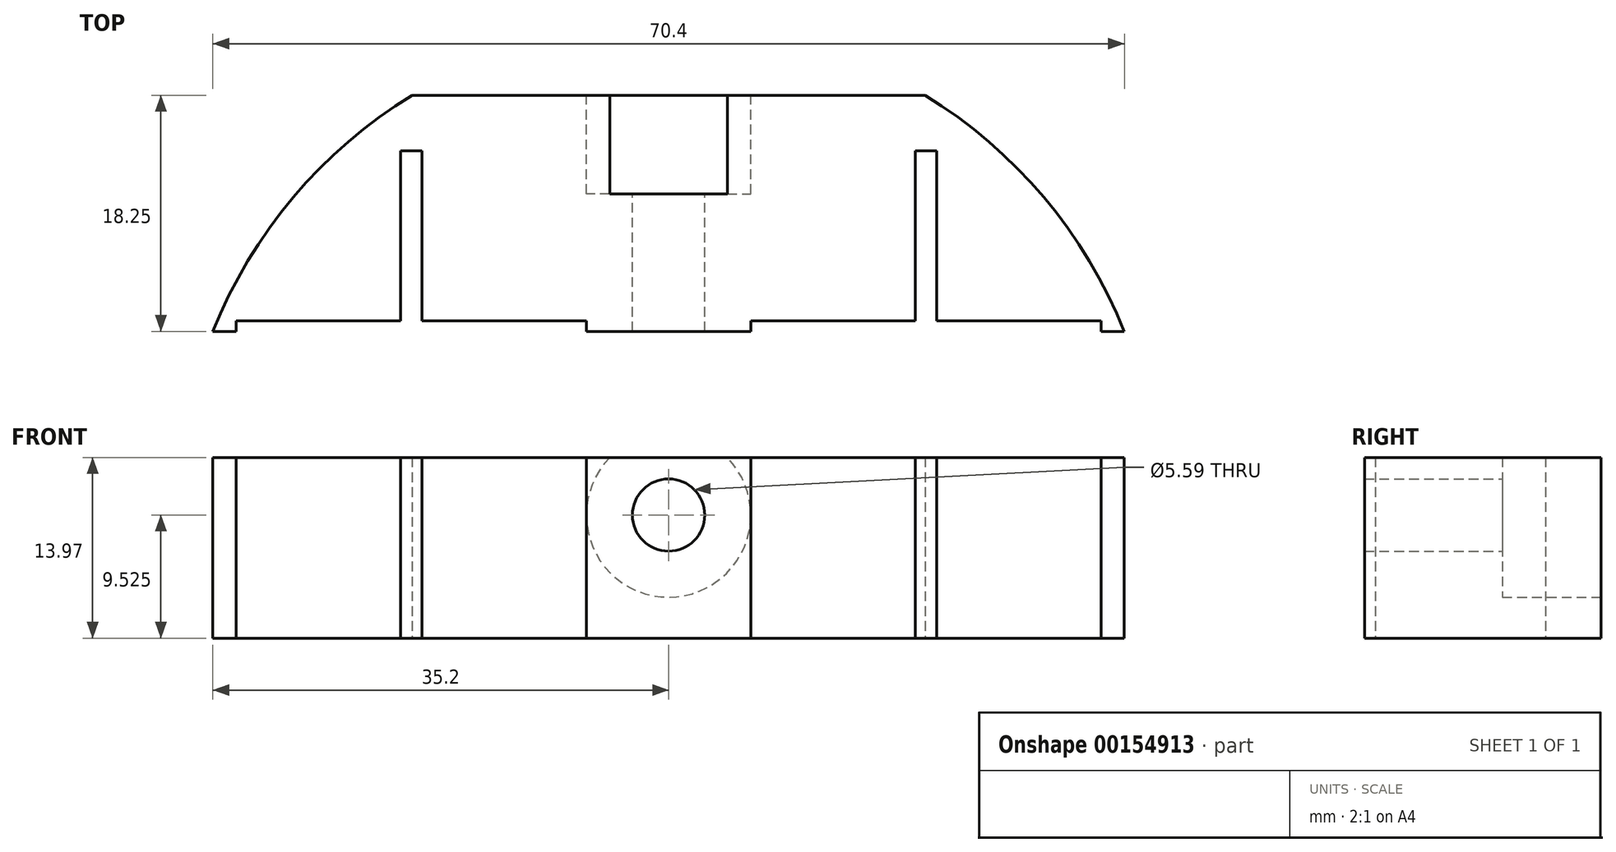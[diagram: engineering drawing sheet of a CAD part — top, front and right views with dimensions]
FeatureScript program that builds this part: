
annotation { "Feature Type Name" : "Feature", "Feature Type Description" : "" }
export const myFeature = defineFeature(function(context is Context, id is Id, definition is map)
    precondition{}
    {
        {
            var Q0;
            Q0=qCreatedBy(makeId("Top.planeOp"),FACE);
            var sketch = newSketch(context, id + "F0", { "sketchPlane" : qUnion([Q0])});
            skArc(sketch, "E0", {"start": v(-19.82, 32.3) * mm, "mid": v(-28.98, 24.42) * mm, "end": v(-35.2, 14.05) * mm});
            skLineSegment(sketch, "E1", {"start": v(-35.2, 14.05) * mm, "end": v(-33.4, 14.05) * mm});
            skLineSegment(sketch, "E2", {"start": v(0, 14.05) * mm, "end": v(0, 32.3) * mm});
            skLineSegment(sketch, "E3", {"start": v(-19.82, 32.3) * mm, "end": v(0, 32.3) * mm});
            skLineSegment(sketch, "E4", {"start": v(-33.4, 14.05) * mm, "end": v(-33.4, 14.87) * mm});
            skLineSegment(sketch, "E5", {"start": v(-33.4, 14.87) * mm, "end": v(-20.7, 14.87) * mm});
            skLineSegment(sketch, "E6", {"start": v(-20.7, 14.87) * mm, "end": v(-20.7, 28.02) * mm});
            skLineSegment(sketch, "E7", {"start": v(-20.7, 28.02) * mm, "end": v(-19.05, 28.02) * mm});
            skLineSegment(sketch, "E8", {"start": v(-19.05, 28.02) * mm, "end": v(-19.05, 14.87) * mm});
            skLineSegment(sketch, "E9", {"start": v(-19.05, 14.87) * mm, "end": v(-6.35, 14.87) * mm});
            skLineSegment(sketch, "E10", {"start": v(-6.35, 14.87) * mm, "end": v(-6.35, 14.05) * mm});
            skLineSegment(sketch, "E11.trimOffspring", {"start": v(-6.35, 14.05) * mm, "end": v(0, 14.05) * mm});
            skSolve(sketch);
        }
        {
            var Q0;
            Q0=makeQuery(id+"F0.imprint","IMPRINT",FACE,{"disambiguationData":[TD([[makeQuery(id+"F0.imprint","IMPRINT",EDGE,{"derivedFrom":sQuery(id+"F0.wireOp",EDGE,"E0")}),1.0]])]});
            extrude(context, id + "F1", {"entities" : qUnion([Q0]), "depth" : 19.05 * mm});
        }
        {
            var Q0;
            Q0=makeQuery(id+"F1.opExtrude","SWEPT_BODY",BODY,{"disambiguationData":[OSD([sQuery(id+"F0.wireOp",EDGE,"E0"),sQuery(id+"F0.wireOp",EDGE,"E1"),sQuery(id+"F0.wireOp",EDGE,"E2"),sQuery(id+"F0.wireOp",EDGE,"E3"),sQuery(id+"F0.wireOp",EDGE,"E4"),sQuery(id+"F0.wireOp",EDGE,"E5"),sQuery(id+"F0.wireOp",EDGE,"E6"),sQuery(id+"F0.wireOp",EDGE,"E7"),sQuery(id+"F0.wireOp",EDGE,"E8"),sQuery(id+"F0.wireOp",EDGE,"E9"),sQuery(id+"F0.wireOp",EDGE,"E10"),sQuery(id+"F0.wireOp",EDGE,"E11.trimOffspring")])]});
            var Q1;
            Q1=qCreatedBy(makeId("Right.planeOp"),FACE);
            mirror(context, id + "F2", {"operationType" : NewBodyOperationType.ADD, "entities" : qUnion([Q0]), "mirrorPlane" : qUnion([Q1])});
        }
        {
            var Q0;
            {var subQ0=makeQuery(id+"F1.opExtrude","SWEPT_FACE",FACE,{"disambiguationData":[OSD([sQuery(id+"F0.wireOp",EDGE,"E3")])]});Q0=makeQuery(id+"F2.boolean.opBoolean","MERGE",FACE,{"derivedFrom":[subQ0,makeQuery(id+"F2.opPattern","COPY",FACE,{"derivedFrom":subQ0,"instanceName":"1"})]});}
            var sketch = newSketch(context, id + "F3", { "sketchPlane" : qUnion([Q0])});
            skLineSegment(sketch, "E12", {"start": v(0, 19.05) * mm, "end": v(0, 0) * mm, "construction": true});
            skLineSegment(sketch, "E13", {"start": v(19.82, 9.53) * mm, "end": v(-19.82, 9.53) * mm, "construction": true});
            skCircle(sketch, "E14", {"center": v(0, 9.53) * mm, "radius": 2.8 * mm});
            skSolve(sketch);
        }
        {
            var Q0;
            Q0 = qSketchRegion(id + "F3", true);
            extrude(context, id + "F4", {"entities" : qUnion([Q0]), "operationType" : NewBodyOperationType.REMOVE, "endBound" : BoundingType.UP_TO_NEXT, "oppositeDirection" : true, "depth" : 25.4 * mm});
        }
        {
            var Q0;
            {var subQ0=makeQuery(id+"F1.opExtrude","SWEPT_FACE",FACE,{"disambiguationData":[OSD([sQuery(id+"F0.wireOp",EDGE,"E3")])]});Q0=makeQuery(id+"F2.boolean.opBoolean","MERGE",FACE,{"derivedFrom":[subQ0,makeQuery(id+"F2.opPattern","COPY",FACE,{"derivedFrom":subQ0,"instanceName":"1"})]});}
            var sketch = newSketch(context, id + "F5", { "sketchPlane" : qUnion([Q0])});
            skCircle(sketch, "E15", {"center": v(0, 9.53) * mm, "radius": 6.35 * mm});
            skSolve(sketch);
        }
        {
            var Q0;
            Q0 = qSketchRegion(id + "F5", true);
            extrude(context, id + "F6", {"entities" : qUnion([Q0]), "operationType" : NewBodyOperationType.REMOVE, "oppositeDirection" : true, "depth" : 7.62 * mm});
        }
        {
            var Q0;
            {var subQ0=makeQuery(id+"F1.opExtrude","CAP_FACE",FACE,{"disambiguationData":[OSD([sQuery(id+"F0.wireOp",EDGE,"E0"),sQuery(id+"F0.wireOp",EDGE,"E1"),sQuery(id+"F0.wireOp",EDGE,"E2"),sQuery(id+"F0.wireOp",EDGE,"E3"),sQuery(id+"F0.wireOp",EDGE,"E4"),sQuery(id+"F0.wireOp",EDGE,"E5"),sQuery(id+"F0.wireOp",EDGE,"E6"),sQuery(id+"F0.wireOp",EDGE,"E7"),sQuery(id+"F0.wireOp",EDGE,"E8"),sQuery(id+"F0.wireOp",EDGE,"E9"),sQuery(id+"F0.wireOp",EDGE,"E10"),sQuery(id+"F0.wireOp",EDGE,"E11.trimOffspring")])],"isStart":false});Q0=makeQuery(id+"F2.boolean.opBoolean","MERGE",FACE,{"derivedFrom":[subQ0,makeQuery(id+"F2.opPattern","COPY",FACE,{"derivedFrom":subQ0,"instanceName":"1"})]});}
            var sketch = newSketch(context, id + "F7", { "sketchPlane" : qUnion([Q0])});
            skLineSegment(sketch, "E16.bottom", {"start": v(-40.23, 33.9) * mm, "end": v(42.4, 33.9) * mm});
            skLineSegment(sketch, "E16.top", {"start": v(-40.23, 12.44) * mm, "end": v(42.4, 12.44) * mm});
            skLineSegment(sketch, "E16.left", {"start": v(-40.23, 33.9) * mm, "end": v(-40.23, 12.44) * mm});
            skLineSegment(sketch, "E16.right", {"start": v(42.4, 33.9) * mm, "end": v(42.4, 12.44) * mm});
            skSolve(sketch);
        }
        {
            var Q0;
            Q0 = qSketchRegion(id + "F7", true);
            extrude(context, id + "F8", {"entities" : qUnion([Q0]), "operationType" : NewBodyOperationType.REMOVE, "oppositeDirection" : true, "depth" : 5.08 * mm});
        }
    });
